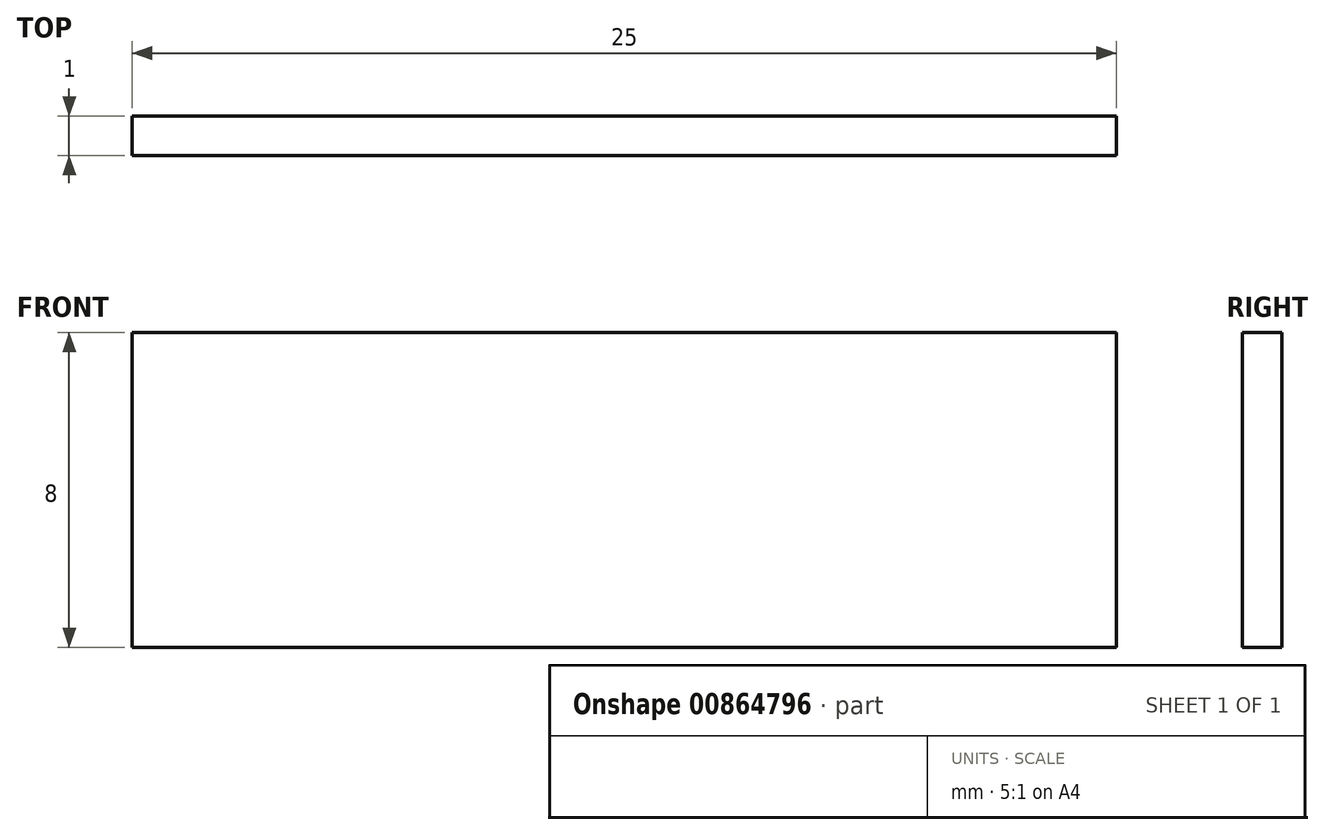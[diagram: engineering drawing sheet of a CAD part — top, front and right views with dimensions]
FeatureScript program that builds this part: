
annotation { "Feature Type Name" : "Feature", "Feature Type Description" : "" }
export const myFeature = defineFeature(function(context is Context, id is Id, definition is map)
    precondition{}
    {
        {
            var Q0;
            Q0=qCreatedBy(makeId("Front.planeOp"),FACE);
            var sketch = newSketch(context, id + "F0", { "sketchPlane" : qUnion([Q0])});
            skLineSegment(sketch, "E0.bottom", {"start": v(0, 0) * mm, "end": v(25, 0) * mm});
            skLineSegment(sketch, "E0.top", {"start": v(0, 8) * mm, "end": v(25, 8) * mm});
            skLineSegment(sketch, "E0.left", {"start": v(0, 0) * mm, "end": v(0, 8) * mm});
            skLineSegment(sketch, "E0.right", {"start": v(25, 0) * mm, "end": v(25, 8) * mm});
            skSolve(sketch);
        }
        {
            var Q0;
            Q0=makeQuery(id+"F0.imprint","IMPRINT",FACE,{"disambiguationData":[TD([[makeQuery(id+"F0.imprint","IMPRINT",EDGE,{"derivedFrom":sQuery(id+"F0.wireOp",EDGE,"E0.bottom")}),1.0]])]});
            extrude(context, id + "F1", {"entities" : qUnion([Q0]), "depth" : 1 * mm, "offsetDistance" : 25 * mm});
        }
    });
